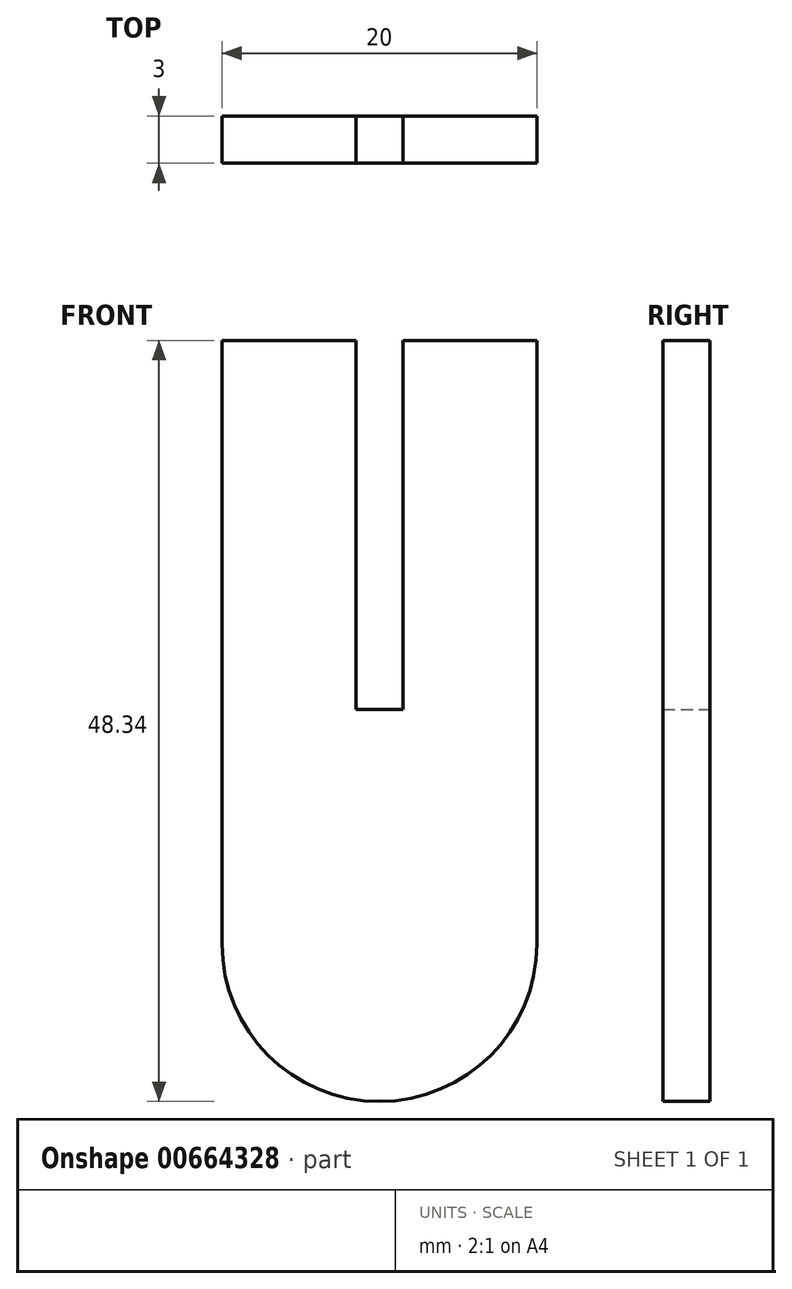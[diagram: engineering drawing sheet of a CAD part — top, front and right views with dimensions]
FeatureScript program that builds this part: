
annotation { "Feature Type Name" : "Feature", "Feature Type Description" : "" }
export const myFeature = defineFeature(function(context is Context, id is Id, definition is map)
    precondition{}
    {
        {
            var Q0;
            Q0=qCreatedBy(makeId("Front.planeOp"),FACE);
            var sketch = newSketch(context, id + "F0", { "sketchPlane" : qUnion([Q0])});
            skLineSegment(sketch, "E0", {"start": v(-25.28, 38.34) * mm, "end": v(-25.28, 0) * mm});
            skLineSegment(sketch, "E1", {"start": v(-5.28, 0) * mm, "end": v(-5.28, 38.34) * mm});
            skLineSegment(sketch, "E2", {"start": v(-5.28, 38.34) * mm, "end": v(-13.78, 38.34) * mm});
            skArc(sketch, "E3", {"start": v(-25.28, 0) * mm, "mid": v(-15.28, -10) * mm, "end": v(-5.28, 0) * mm});
            skLineSegment(sketch, "E4", {"start": v(-13.78, 38.34) * mm, "end": v(-13.78, 14.9) * mm});
            skLineSegment(sketch, "E5", {"start": v(-13.78, 14.9) * mm, "end": v(-16.78, 14.9) * mm});
            skLineSegment(sketch, "E6", {"start": v(-16.78, 14.9) * mm, "end": v(-16.78, 38.34) * mm});
            skLineSegment(sketch, "E7.trimOffspring", {"start": v(-16.78, 38.34) * mm, "end": v(-25.28, 38.34) * mm});
            skSolve(sketch);
        }
        {
            var Q0;
            Q0=makeQuery(id+"F0.imprint","IMPRINT",FACE,{"disambiguationData":[TD([[makeQuery(id+"F0.imprint","IMPRINT",EDGE,{"derivedFrom":sQuery(id+"F0.wireOp",EDGE,"E0")}),1.0]])]});
            extrude(context, id + "F1", {"entities" : qUnion([Q0]), "depth" : 3 * mm, "offsetDistance" : 25 * mm});
        }
    });
